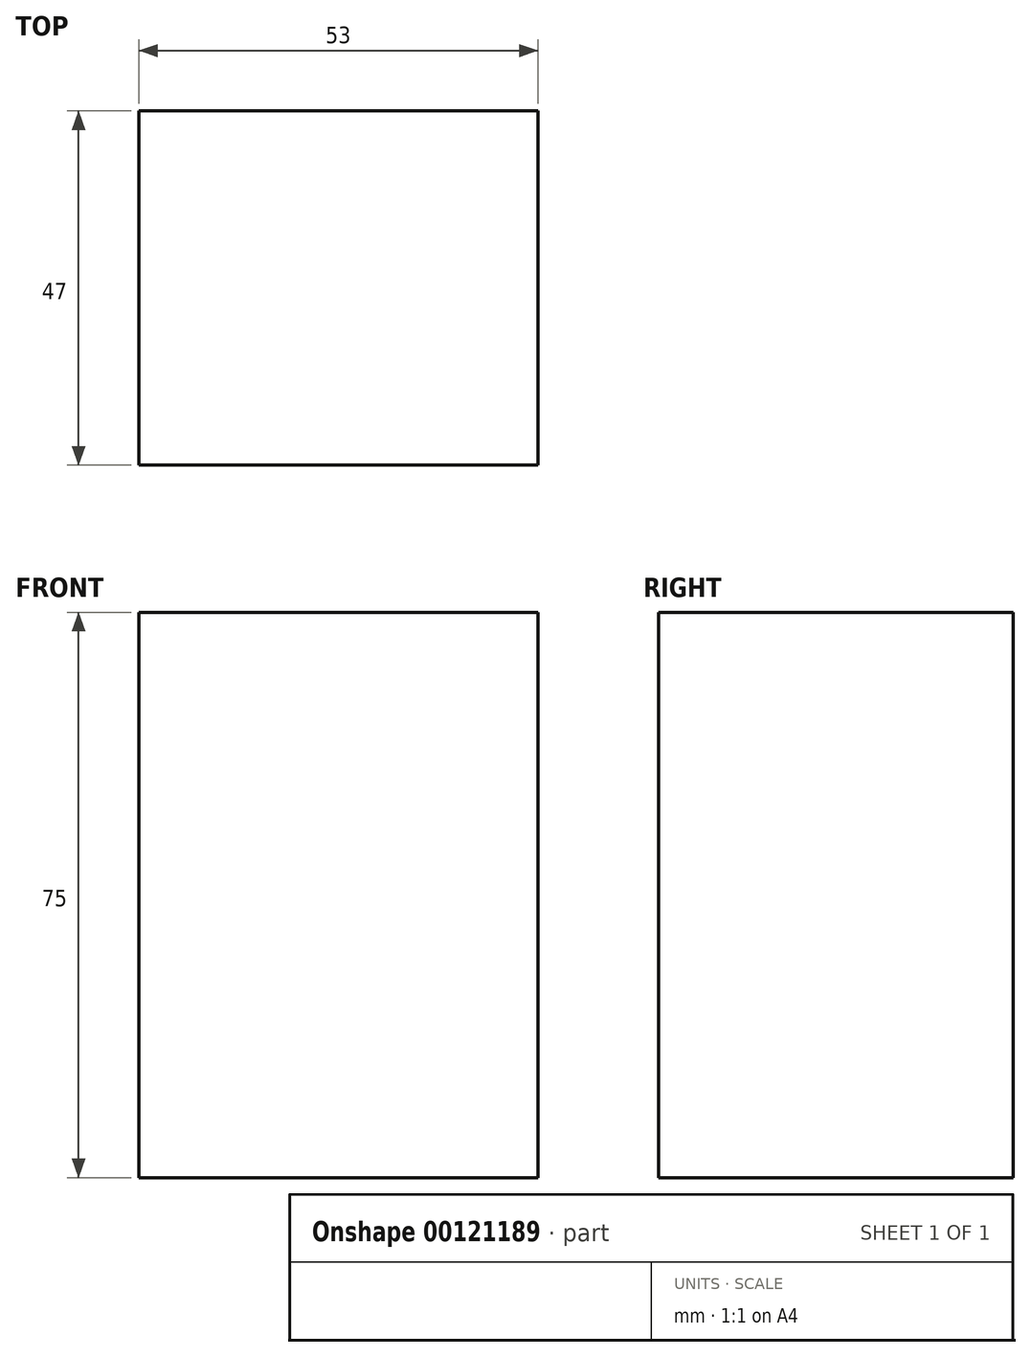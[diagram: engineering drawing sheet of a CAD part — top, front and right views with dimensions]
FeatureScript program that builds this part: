
annotation { "Feature Type Name" : "Feature", "Feature Type Description" : "" }
export const myFeature = defineFeature(function(context is Context, id is Id, definition is map)
    precondition{}
    {
        {
            var Q0;
            Q0=qCreatedBy(makeId("Front.planeOp"),FACE);
            var sketch = newSketch(context, id + "F0", { "sketchPlane" : qUnion([Q0])});
            skLineSegment(sketch, "E0.bottom", {"start": v(26.5, -37.5) * mm, "end": v(-26.5, -37.5) * mm});
            skLineSegment(sketch, "E0.top", {"start": v(26.5, 37.5) * mm, "end": v(-26.5, 37.5) * mm});
            skLineSegment(sketch, "E0.left", {"start": v(26.5, -37.5) * mm, "end": v(26.5, 37.5) * mm});
            skLineSegment(sketch, "E0.right", {"start": v(-26.5, -37.5) * mm, "end": v(-26.5, 37.5) * mm});
            skPoint(sketch, "E0.middle", {"position": v(0, 0) * mm});
            skSolve(sketch);
        }
        {
            var Q0;
            Q0 = qSketchRegion(id + "F0", true);
            extrude(context, id + "F1", {"entities" : qUnion([Q0]), "depth" : 47 * mm});
        }
    });
